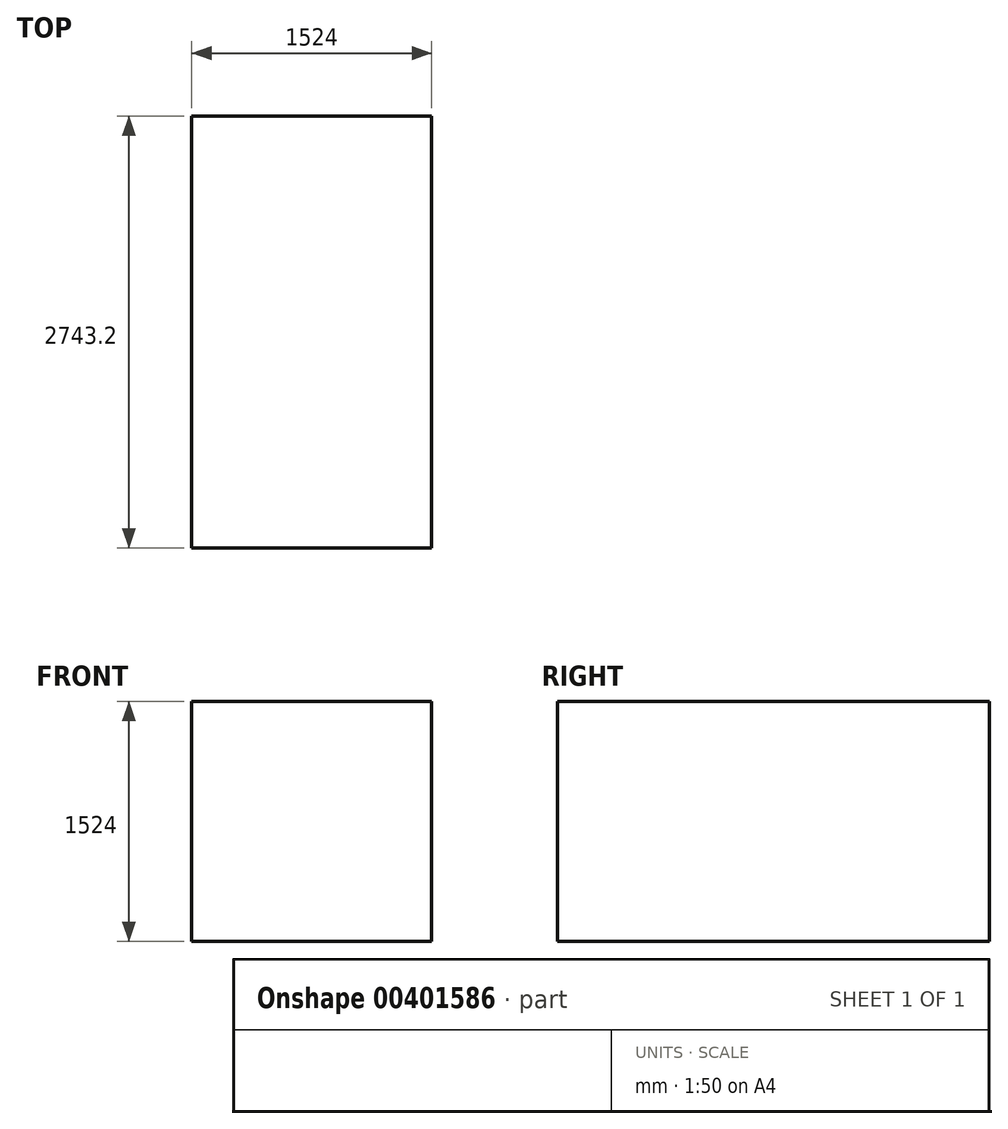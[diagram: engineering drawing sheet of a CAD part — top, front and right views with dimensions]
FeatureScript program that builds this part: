
annotation { "Feature Type Name" : "Feature", "Feature Type Description" : "" }
export const myFeature = defineFeature(function(context is Context, id is Id, definition is map)
    precondition{}
    {
        {
            var Q0;
            Q0=qCreatedBy(makeId("Front.planeOp"),FACE);
            var sketch = newSketch(context, id + "F0", { "sketchPlane" : qUnion([Q0])});
            skLineSegment(sketch, "E0.bottom", {"start": v(-762, 0) * mm, "end": v(762, 0) * mm});
            skLineSegment(sketch, "E0.top", {"start": v(-762, 1524) * mm, "end": v(762, 1524) * mm});
            skLineSegment(sketch, "E0.left", {"start": v(-762, 0) * mm, "end": v(-762, 1524) * mm});
            skLineSegment(sketch, "E0.right", {"start": v(762, 0) * mm, "end": v(762, 1524) * mm});
            skSolve(sketch);
        }
        {
            var Q0;
            Q0 = qSketchRegion(id + "F0", true);
            extrude(context, id + "F1", {"entities" : qUnion([Q0]), "oppositeDirection" : true, "depth" : 2743.2 * mm});
        }
    });
